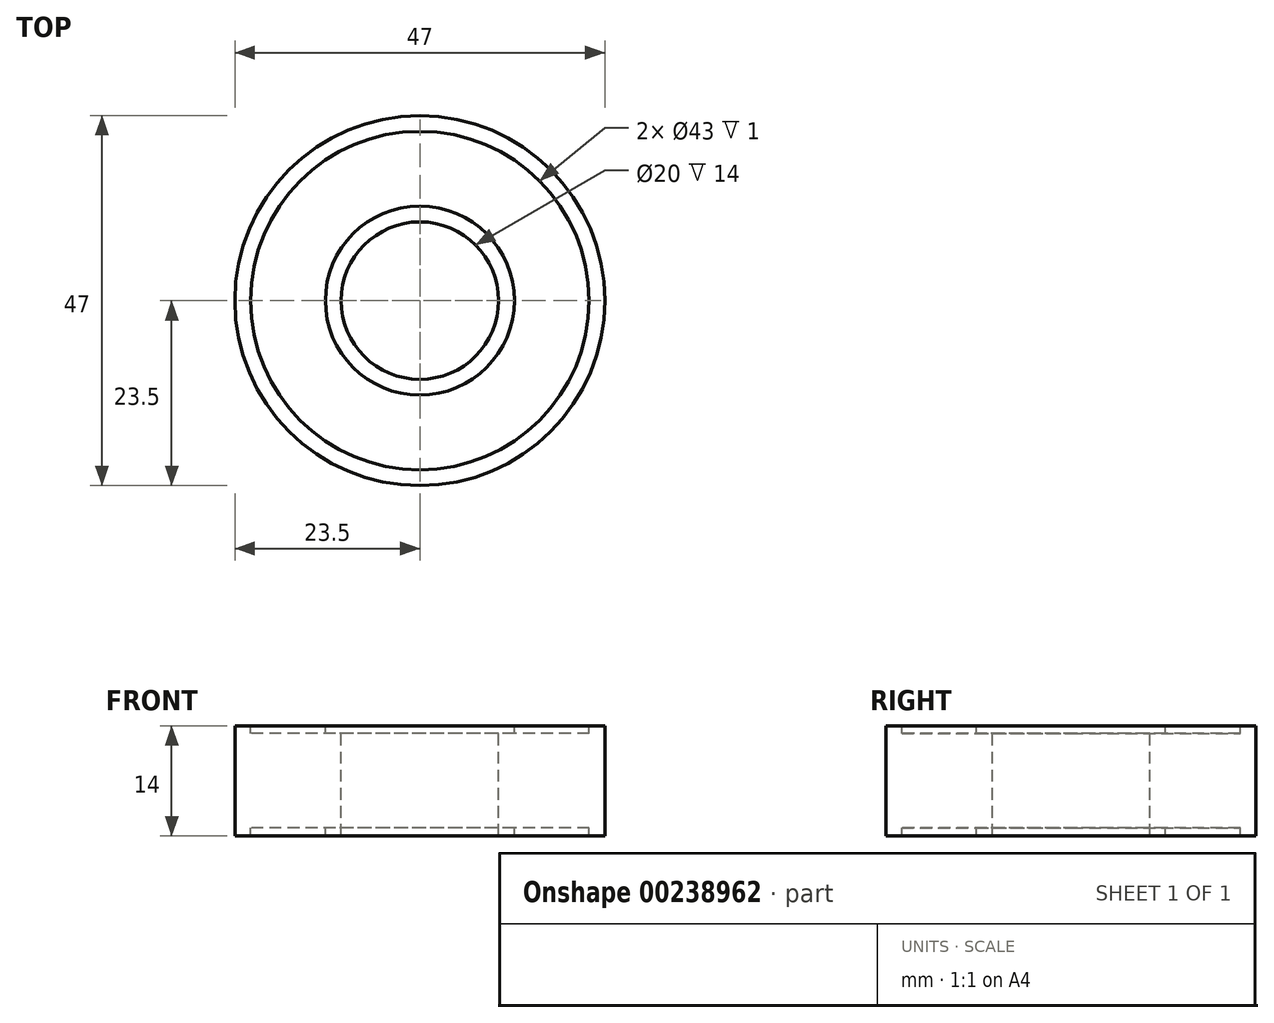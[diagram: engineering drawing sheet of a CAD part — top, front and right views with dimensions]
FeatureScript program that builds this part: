
annotation { "Feature Type Name" : "Feature", "Feature Type Description" : "" }
export const myFeature = defineFeature(function(context is Context, id is Id, definition is map)
    precondition{}
    {
        {
            var Q0;
            Q0=qCreatedBy(makeId("Front.planeOp"),FACE);
            var sketch = newSketch(context, id + "F0", { "sketchPlane" : qUnion([Q0])});
            skLineSegment(sketch, "E0.MirrorCS", {"start": v(-21.5, -6) * mm, "end": v(-12, -6) * mm});
            skLineSegment(sketch, "E1.MirrorCS", {"start": v(-21.5, -7) * mm, "end": v(-23.5, -7) * mm});
            skLineSegment(sketch, "E2.MirrorCS", {"start": v(-12, -7) * mm, "end": v(-12, -6) * mm});
            skLineSegment(sketch, "E3.MirrorCS", {"start": v(-21.5, -7) * mm, "end": v(-21.5, -6) * mm});
            skLineSegment(sketch, "E4.MirrorCS", {"start": v(-10, -7) * mm, "end": v(-12, -7) * mm});
            skLineSegment(sketch, "E5.MirrorCS", {"start": v(-21.5, 7) * mm, "end": v(-23.5, 7) * mm});
            skLineSegment(sketch, "E6.MirrorCS", {"start": v(-10, 7) * mm, "end": v(-12, 7) * mm});
            skLineSegment(sketch, "E7.MirrorCS", {"start": v(-21.5, 7) * mm, "end": v(-21.5, 6) * mm});
            skLineSegment(sketch, "E8.MirrorCS", {"start": v(-12, 7) * mm, "end": v(-12, 6) * mm});
            skLineSegment(sketch, "E9.MirrorCS", {"start": v(-21.5, 6) * mm, "end": v(-12, 6) * mm});
            skLineSegment(sketch, "E10", {"start": v(-10, -7) * mm, "end": v(-10, 0) * mm});
            skLineSegment(sketch, "E11", {"start": v(-23.5, -7) * mm, "end": v(-23.5, 0) * mm});
            skLineSegment(sketch, "E12.MirrorCS", {"start": v(-23.5, 7) * mm, "end": v(-23.5, 0) * mm});
            skLineSegment(sketch, "E13.MirrorCS", {"start": v(-10, 7) * mm, "end": v(-10, 0) * mm});
            skLineSegment(sketch, "E14", {"start": v(0, 9.56) * mm, "end": v(0, -9.15) * mm, "construction": true});
            skSolve(sketch);
        }
        {
            var Q0;
            Q0=qSketchRegion(id+"F0",true);
            var Q1;
            Q1=sQuery(id+"F0.wireOp",EDGE,"E14");
            revolve(context, id + "F1", {"entities" : qUnion([Q0]), "axis" : qUnion([Q1]), "revolveType" : RevolveType.FULL});
        }
    });
